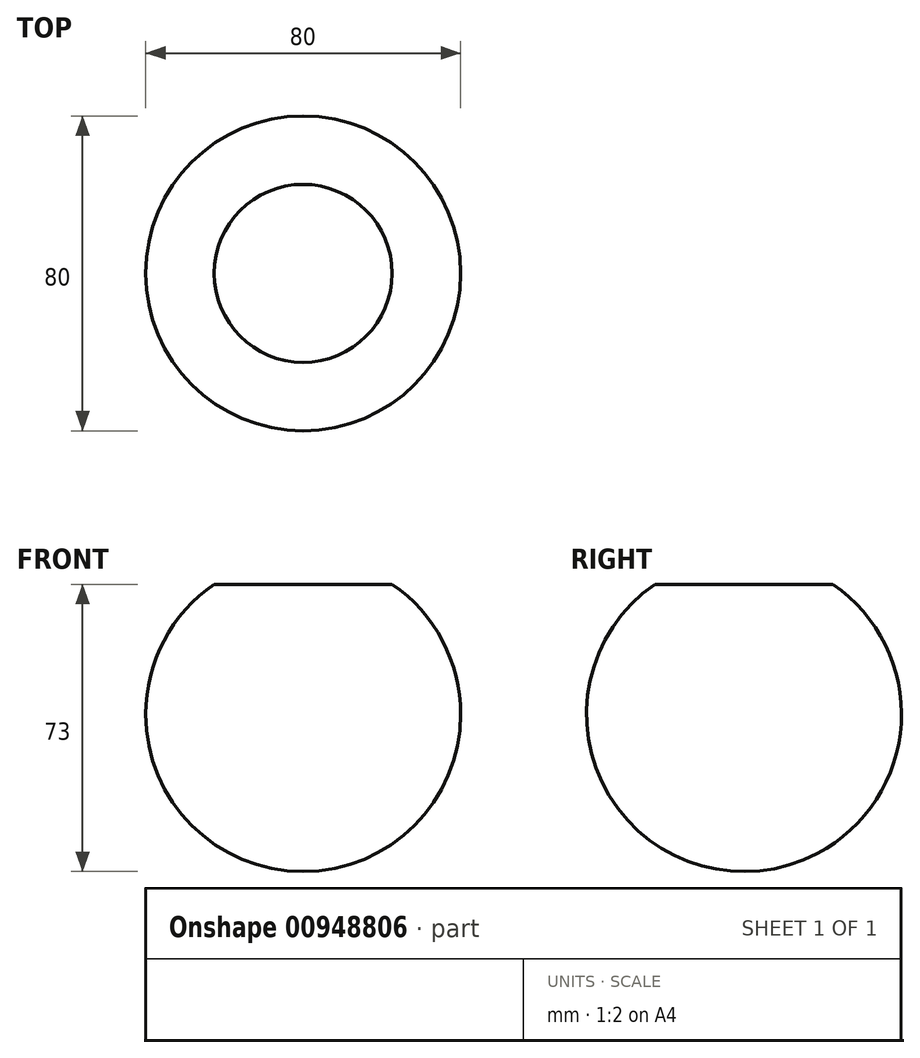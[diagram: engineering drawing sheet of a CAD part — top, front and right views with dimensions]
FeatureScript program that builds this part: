
annotation { "Feature Type Name" : "Feature", "Feature Type Description" : "" }
export const myFeature = defineFeature(function(context is Context, id is Id, definition is map)
    precondition{}
    {
        {
            var Q0;
            Q0=qCreatedBy(makeId("Top.planeOp"),FACE);
            var sketch = newSketch(context, id + "F0", { "sketchPlane" : qUnion([Q0])});
            skLineSegment(sketch, "E0", {"start": v(0, 0) * mm, "end": v(-50, 0) * mm, "construction": true});
            skLineSegment(sketch, "E1.1.0", {"start": v(0, 0) * mm, "end": v(0, -50) * mm, "construction": true});
            skLineSegment(sketch, "E1.2.0", {"start": v(0, 0) * mm, "end": v(50, 0) * mm, "construction": true});
            skLineSegment(sketch, "E1.3.0", {"start": v(0, 0) * mm, "end": v(0, 50) * mm, "construction": true});
            skPoint(sketch, "E1.center", {"position": v(0, 0) * mm});
            skArc(sketch, "E2", {"start": v(40, 0) * mm, "mid": v(0, 40) * mm, "end": v(-40, 0) * mm});
            skLineSegment(sketch, "E3", {"start": v(-40, 0) * mm, "end": v(40, 0) * mm});
            skSolve(sketch);
        }
        {
            var Q0;
            Q0=makeQuery(id+"F0.imprint","IMPRINT",FACE,{"disambiguationData":[TD([[makeQuery(id+"F0.imprint","IMPRINT",EDGE,{"derivedFrom":sQuery(id+"F0.wireOp",EDGE,"E2")}),1.0]])]});
            var Q1;
            Q1=sQuery(id+"F0.wireOp",EDGE,"E2");
            var Q2;
            Q2=sQuery(id+"F0.wireOp",EDGE,"E0");
            revolve(context, id + "F1", {"surfaceOperationType" : NewSurfaceOperationType.NEW, "entities" : qUnion([Q0]), "surfaceEntities" : qUnion([Q1]), "axis" : qUnion([Q2]), "revolveType" : RevolveType.FULL});
        }
        {
            var Q0;
            Q0=qCreatedBy(makeId("Top.planeOp"),FACE);
            cPlane(context, id + "F2", {"entities" : qUnion([Q0]), "cplaneType" : CPlaneType.OFFSET, "offset" : 33 * mm, "width" : 150 * mm, "height" : 150 * mm});
        }
        {
            var Q0;
            Q0=qCreatedBy(id+"F2.planeOp",FACE);
            var sketch = newSketch(context, id + "F3", { "sketchPlane" : qUnion([Q0])});
            skCircle(sketch, "E4", {"center": v(0, 0) * mm, "radius": 22.6 * mm});
            skSolve(sketch);
        }
        {
            var Q0;
            Q0 = qSketchRegion(id + "F3", true);
            var Q1;
            Q1=makeQuery(id+"F1.opRevolve","SWEPT_BODY",BODY,{"disambiguationData":[OSD([sQuery(id+"F0.wireOp",EDGE,"E2"),sQuery(id+"F0.wireOp",EDGE,"E3")])]});
            extrude(context, id + "F4", {"entities" : qUnion([Q0]), "operationType" : NewBodyOperationType.REMOVE, "endBound" : BoundingType.UP_TO_BODY, "depth" : 25 * mm, "endBoundEntityBody" : qUnion([Q1]), "offsetDistance" : 25 * mm});
        }
    });
